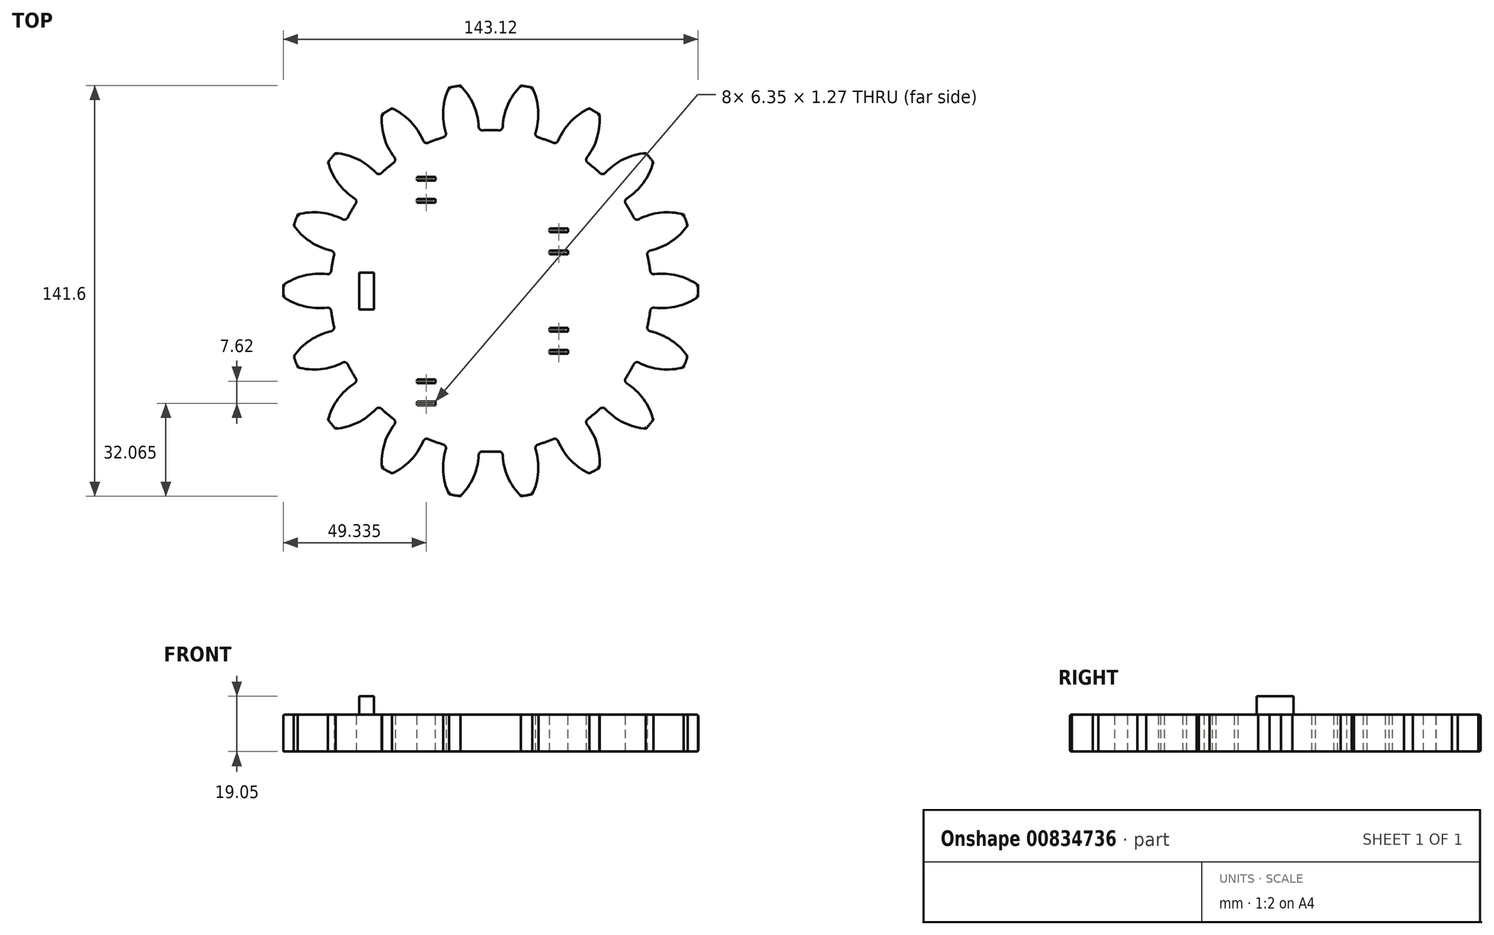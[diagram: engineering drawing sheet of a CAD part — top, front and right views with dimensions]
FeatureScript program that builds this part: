
annotation { "Feature Type Name" : "Feature", "Feature Type Description" : "" }
export const myFeature = defineFeature(function(context is Context, id is Id, definition is map)
    precondition{}
    {
        {
            var Q0;
            Q0=qCreatedBy(makeId("Top.planeOp"),FACE);
            var sketch = newSketch(context, id + "F0", { "sketchPlane" : qUnion([Q0])});
            skCircle(sketch, "E0", {"center": v(0, 0) * mm, "radius": 10.58 * mm});
            skCircle(sketch, "E1", {"center": v(0, 0) * mm, "radius": 21.17 * mm});
            skCircle(sketch, "E2", {"center": v(0, 0) * mm, "radius": 42.33 * mm});
            skArc(sketch, "E3.0", {"start": v(71.54, -1.99) * mm, "mid": v(71.56, 0) * mm, "end": v(71.54, 1.99) * mm});
            skArc(sketch, "E4.trimOffspring", {"start": v(2.79, 55.37) * mm, "mid": v(0, 55.44) * mm, "end": v(-2.79, 55.37) * mm});
            skPoint(sketch, "E5.orphan", {"position": v(0, 102.8) * mm});
            skArc(sketch, "E6.1.0", {"start": v(-16.32, 52.98) * mm, "mid": v(-18.96, 52.1) * mm, "end": v(-21.56, 51.07) * mm});
            skArc(sketch, "E6.2.0", {"start": v(-33.45, 44.2) * mm, "mid": v(-35.63, 42.47) * mm, "end": v(-37.72, 40.62) * mm});
            skArc(sketch, "E7.3.3.0", {"start": v(-46.55, 30.1) * mm, "mid": v(-48, 27.72) * mm, "end": v(-49.34, 25.27) * mm});
            skArc(sketch, "E7.3.4.0", {"start": v(-54.04, 12.36) * mm, "mid": v(-54.6, 9.63) * mm, "end": v(-55, 6.87) * mm});
            skArc(sketch, "E7.3.5.0", {"start": v(-55, -6.87) * mm, "mid": v(-54.6, -9.63) * mm, "end": v(-54.04, -12.36) * mm});
            skArc(sketch, "E7.3.6.0", {"start": v(-49.34, -25.27) * mm, "mid": v(-48, -27.72) * mm, "end": v(-46.55, -30.1) * mm});
            skArc(sketch, "E7.3.7.0", {"start": v(-37.72, -40.62) * mm, "mid": v(-35.63, -42.47) * mm, "end": v(-33.45, -44.2) * mm});
            skArc(sketch, "E7.3.8.0", {"start": v(-21.56, -51.07) * mm, "mid": v(-18.96, -52.1) * mm, "end": v(-16.32, -52.98) * mm});
            skArc(sketch, "E7.3.9.0", {"start": v(-2.79, -55.37) * mm, "mid": v(0, -55.44) * mm, "end": v(2.79, -55.37) * mm});
            skArc(sketch, "E7.3.10.0", {"start": v(16.32, -52.98) * mm, "mid": v(18.96, -52.1) * mm, "end": v(21.56, -51.07) * mm});
            skArc(sketch, "E7.3.11.0", {"start": v(33.45, -44.2) * mm, "mid": v(35.63, -42.47) * mm, "end": v(37.72, -40.62) * mm});
            skArc(sketch, "E7.3.12.0", {"start": v(46.55, -30.1) * mm, "mid": v(48, -27.72) * mm, "end": v(49.34, -25.27) * mm});
            skArc(sketch, "E7.3.13.0", {"start": v(54.04, -12.36) * mm, "mid": v(54.6, -9.63) * mm, "end": v(55, -6.87) * mm});
            skArc(sketch, "E7.3.14.0", {"start": v(55, 6.87) * mm, "mid": v(54.6, 9.63) * mm, "end": v(54.04, 12.36) * mm});
            skArc(sketch, "E7.3.15.0", {"start": v(49.34, 25.27) * mm, "mid": v(48, 27.72) * mm, "end": v(46.55, 30.1) * mm});
            skArc(sketch, "E7.3.16.0", {"start": v(37.72, 40.62) * mm, "mid": v(35.63, 42.47) * mm, "end": v(33.45, 44.2) * mm});
            skArc(sketch, "E7.3.17.0", {"start": v(21.56, 51.07) * mm, "mid": v(18.96, 52.1) * mm, "end": v(16.32, 52.98) * mm});
            skArc(sketch, "E8", {"start": v(71.54, 1.99) * mm, "mid": v(64.35, 5.3) * mm, "end": v(56.45, 5.75) * mm});
            skArc(sketch, "E9", {"start": v(56.45, -5.75) * mm, "mid": v(64.35, -5.3) * mm, "end": v(71.54, -1.99) * mm});
            skArc(sketch, "E10.1.0", {"start": v(55.02, 13.9) * mm, "mid": v(62.28, 17.03) * mm, "end": v(67.9, 22.6) * mm});
            skArc(sketch, "E10.1.1", {"start": v(67.9, 22.6) * mm, "mid": v(67.25, 24.48) * mm, "end": v(66.54, 26.34) * mm});
            skArc(sketch, "E10.1.2", {"start": v(66.54, 26.34) * mm, "mid": v(58.66, 26.99) * mm, "end": v(51.08, 24.71) * mm});
            skArc(sketch, "E10.2.0", {"start": v(46.94, 31.88) * mm, "mid": v(52.7, 37.3) * mm, "end": v(56.08, 44.46) * mm});
            skArc(sketch, "E10.2.1", {"start": v(56.08, 44.46) * mm, "mid": v(54.82, 46) * mm, "end": v(53.52, 47.5) * mm});
            skArc(sketch, "E10.2.2", {"start": v(53.52, 47.5) * mm, "mid": v(45.89, 45.42) * mm, "end": v(39.55, 40.7) * mm});
            skArc(sketch, "E10.3.0", {"start": v(33.2, 46.01) * mm, "mid": v(36.77, 53.08) * mm, "end": v(37.5, 60.96) * mm});
            skArc(sketch, "E10.3.1", {"start": v(37.5, 60.96) * mm, "mid": v(35.78, 61.98) * mm, "end": v(34.05, 62.95) * mm});
            skArc(sketch, "E10.3.2", {"start": v(34.05, 62.95) * mm, "mid": v(27.59, 58.38) * mm, "end": v(23.24, 51.77) * mm});
            skArc(sketch, "E10.4.0", {"start": v(15.47, 54.6) * mm, "mid": v(16.4, 62.45) * mm, "end": v(14.38, 70.1) * mm});
            skArc(sketch, "E10.4.1", {"start": v(14.38, 70.1) * mm, "mid": v(12.43, 70.48) * mm, "end": v(10.46, 70.8) * mm});
            skArc(sketch, "E10.4.2", {"start": v(10.46, 70.8) * mm, "mid": v(5.95, 64.3) * mm, "end": v(4.14, 56.6) * mm});
            skArc(sketch, "E10.5.0", {"start": v(-4.14, 56.6) * mm, "mid": v(-5.95, 64.3) * mm, "end": v(-10.46, 70.8) * mm});
            skArc(sketch, "E10.5.1", {"start": v(-10.46, 70.8) * mm, "mid": v(-12.43, 70.48) * mm, "end": v(-14.38, 70.1) * mm});
            skArc(sketch, "E10.5.2", {"start": v(-14.38, 70.1) * mm, "mid": v(-16.4, 62.45) * mm, "end": v(-15.47, 54.6) * mm});
            skArc(sketch, "E10.6.0", {"start": v(-23.24, 51.77) * mm, "mid": v(-27.59, 58.38) * mm, "end": v(-34.05, 62.95) * mm});
            skArc(sketch, "E10.6.1", {"start": v(-34.05, 62.95) * mm, "mid": v(-35.78, 61.98) * mm, "end": v(-37.5, 60.96) * mm});
            skArc(sketch, "E10.6.2", {"start": v(-37.5, 60.96) * mm, "mid": v(-36.77, 53.08) * mm, "end": v(-33.2, 46.01) * mm});
            skArc(sketch, "E10.7.0", {"start": v(-39.55, 40.7) * mm, "mid": v(-45.89, 45.42) * mm, "end": v(-53.52, 47.5) * mm});
            skArc(sketch, "E10.7.1", {"start": v(-53.52, 47.5) * mm, "mid": v(-54.82, 46) * mm, "end": v(-56.08, 44.46) * mm});
            skArc(sketch, "E10.7.2", {"start": v(-56.08, 44.46) * mm, "mid": v(-52.7, 37.3) * mm, "end": v(-46.94, 31.88) * mm});
            skArc(sketch, "E10.8.0", {"start": v(-51.08, 24.71) * mm, "mid": v(-58.66, 26.99) * mm, "end": v(-66.54, 26.34) * mm});
            skArc(sketch, "E10.8.1", {"start": v(-66.54, 26.34) * mm, "mid": v(-67.25, 24.48) * mm, "end": v(-67.9, 22.6) * mm});
            skArc(sketch, "E10.8.2", {"start": v(-67.9, 22.6) * mm, "mid": v(-62.28, 17.03) * mm, "end": v(-55.02, 13.9) * mm});
            skArc(sketch, "E10.9.0", {"start": v(-56.45, 5.75) * mm, "mid": v(-64.35, 5.3) * mm, "end": v(-71.54, 1.99) * mm});
            skArc(sketch, "E10.9.1", {"start": v(-71.54, 1.99) * mm, "mid": v(-71.56, 0) * mm, "end": v(-71.54, -1.99) * mm});
            skArc(sketch, "E10.9.2", {"start": v(-71.54, -1.99) * mm, "mid": v(-64.35, -5.3) * mm, "end": v(-56.45, -5.75) * mm});
            skArc(sketch, "E10.10.0", {"start": v(-55.02, -13.9) * mm, "mid": v(-62.28, -17.03) * mm, "end": v(-67.9, -22.6) * mm});
            skArc(sketch, "E10.10.1", {"start": v(-67.9, -22.6) * mm, "mid": v(-67.25, -24.48) * mm, "end": v(-66.54, -26.34) * mm});
            skArc(sketch, "E10.10.2", {"start": v(-66.54, -26.34) * mm, "mid": v(-58.66, -26.99) * mm, "end": v(-51.08, -24.71) * mm});
            skArc(sketch, "E10.11.0", {"start": v(-46.94, -31.88) * mm, "mid": v(-52.7, -37.3) * mm, "end": v(-56.08, -44.46) * mm});
            skArc(sketch, "E10.11.1", {"start": v(-56.08, -44.46) * mm, "mid": v(-54.82, -46) * mm, "end": v(-53.52, -47.5) * mm});
            skArc(sketch, "E10.11.2", {"start": v(-53.52, -47.5) * mm, "mid": v(-45.89, -45.42) * mm, "end": v(-39.55, -40.7) * mm});
            skArc(sketch, "E10.12.0", {"start": v(-33.2, -46.01) * mm, "mid": v(-36.77, -53.08) * mm, "end": v(-37.5, -60.96) * mm});
            skArc(sketch, "E10.12.1", {"start": v(-37.5, -60.96) * mm, "mid": v(-35.78, -61.98) * mm, "end": v(-34.05, -62.95) * mm});
            skArc(sketch, "E10.12.2", {"start": v(-34.05, -62.95) * mm, "mid": v(-27.59, -58.38) * mm, "end": v(-23.24, -51.77) * mm});
            skArc(sketch, "E10.13.0", {"start": v(-15.47, -54.6) * mm, "mid": v(-16.4, -62.45) * mm, "end": v(-14.38, -70.1) * mm});
            skArc(sketch, "E10.13.1", {"start": v(-14.38, -70.1) * mm, "mid": v(-12.43, -70.48) * mm, "end": v(-10.46, -70.8) * mm});
            skArc(sketch, "E10.13.2", {"start": v(-10.46, -70.8) * mm, "mid": v(-5.95, -64.3) * mm, "end": v(-4.14, -56.6) * mm});
            skArc(sketch, "E10.14.0", {"start": v(4.14, -56.6) * mm, "mid": v(5.95, -64.3) * mm, "end": v(10.46, -70.8) * mm});
            skArc(sketch, "E10.14.1", {"start": v(10.46, -70.8) * mm, "mid": v(12.43, -70.48) * mm, "end": v(14.38, -70.1) * mm});
            skArc(sketch, "E10.14.2", {"start": v(14.38, -70.1) * mm, "mid": v(16.4, -62.45) * mm, "end": v(15.47, -54.6) * mm});
            skArc(sketch, "E10.15.0", {"start": v(23.24, -51.77) * mm, "mid": v(27.59, -58.38) * mm, "end": v(34.05, -62.95) * mm});
            skArc(sketch, "E10.15.1", {"start": v(34.05, -62.95) * mm, "mid": v(35.78, -61.98) * mm, "end": v(37.5, -60.96) * mm});
            skArc(sketch, "E10.15.2", {"start": v(37.5, -60.96) * mm, "mid": v(36.77, -53.08) * mm, "end": v(33.2, -46.01) * mm});
            skArc(sketch, "E10.16.0", {"start": v(39.55, -40.7) * mm, "mid": v(45.89, -45.42) * mm, "end": v(53.52, -47.5) * mm});
            skArc(sketch, "E10.16.1", {"start": v(53.52, -47.5) * mm, "mid": v(54.82, -46) * mm, "end": v(56.08, -44.46) * mm});
            skArc(sketch, "E10.16.2", {"start": v(56.08, -44.46) * mm, "mid": v(52.7, -37.3) * mm, "end": v(46.94, -31.88) * mm});
            skArc(sketch, "E10.17.0", {"start": v(51.08, -24.71) * mm, "mid": v(58.66, -26.99) * mm, "end": v(66.54, -26.34) * mm});
            skArc(sketch, "E10.17.1", {"start": v(66.54, -26.34) * mm, "mid": v(67.25, -24.48) * mm, "end": v(67.9, -22.6) * mm});
            skArc(sketch, "E10.17.2", {"start": v(67.9, -22.6) * mm, "mid": v(62.28, -17.03) * mm, "end": v(55.02, -13.9) * mm});
            skPoint(sketch, "E11.newPointA", {"position": v(15.04, 53.36) * mm});
            skPoint(sketch, "E11.newPointB", {"position": v(14.64, 53.47) * mm});
            skArc(sketch, "E11.filletArc", {"start": v(15.47, 54.6) * mm, "mid": v(15.56, 53.61) * mm, "end": v(16.32, 52.98) * mm});
            skPoint(sketch, "E12.newPointA", {"position": v(22.78, 50.54) * mm});
            skPoint(sketch, "E12.newPointB", {"position": v(23.15, 50.37) * mm});
            skArc(sketch, "E12.filletArc", {"start": v(21.56, 51.07) * mm, "mid": v(22.54, 51.07) * mm, "end": v(23.24, 51.77) * mm});
            skPoint(sketch, "E13.newPointA", {"position": v(32.38, 45) * mm});
            skPoint(sketch, "E13.newPointB", {"position": v(32.04, 45.24) * mm});
            skArc(sketch, "E13.filletArc", {"start": v(33.2, 46.01) * mm, "mid": v(32.95, 45.06) * mm, "end": v(33.45, 44.2) * mm});
            skPoint(sketch, "E14.newPointA", {"position": v(38.7, 39.7) * mm});
            skPoint(sketch, "E14.newPointB", {"position": v(38.98, 39.41) * mm});
            skArc(sketch, "E14.filletArc", {"start": v(37.72, 40.62) * mm, "mid": v(38.65, 40.28) * mm, "end": v(39.55, 40.7) * mm});
            skPoint(sketch, "E15.newPointA", {"position": v(45.82, 31.2) * mm});
            skPoint(sketch, "E15.newPointB", {"position": v(45.58, 31.55) * mm});
            skArc(sketch, "E15.filletArc", {"start": v(46.94, 31.88) * mm, "mid": v(46.38, 31.07) * mm, "end": v(46.55, 30.1) * mm});
            skPoint(sketch, "E16.newPointA", {"position": v(50.11, 23.7) * mm});
            skPoint(sketch, "E16.newPointB", {"position": v(49.94, 24.07) * mm});
            skArc(sketch, "E16.filletArc", {"start": v(49.34, 25.27) * mm, "mid": v(50.1, 24.63) * mm, "end": v(51.08, 24.71) * mm});
            skPoint(sketch, "E17.newPointA", {"position": v(53.73, 13.66) * mm});
            skPoint(sketch, "E17.newPointB", {"position": v(53.62, 14.05) * mm});
            skArc(sketch, "E17.filletArc", {"start": v(55.02, 13.9) * mm, "mid": v(54.2, 13.33) * mm, "end": v(54.04, 12.36) * mm});
            skPoint(sketch, "E18.newPointA", {"position": v(55.16, 5.54) * mm});
            skPoint(sketch, "E18.newPointB", {"position": v(55.2, 5.13) * mm});
            skArc(sketch, "E18.filletArc", {"start": v(55, 6.87) * mm, "mid": v(55.5, 6.01) * mm, "end": v(56.45, 5.75) * mm});
            skPoint(sketch, "E19.newPointA", {"position": v(55.16, -5.54) * mm});
            skPoint(sketch, "E19.newPointB", {"position": v(55.2, -5.13) * mm});
            skArc(sketch, "E19.filletArc", {"start": v(56.45, -5.75) * mm, "mid": v(55.5, -6.01) * mm, "end": v(55, -6.87) * mm});
            skPoint(sketch, "E20.newPointA", {"position": v(53.73, -13.66) * mm});
            skPoint(sketch, "E20.newPointB", {"position": v(53.62, -14.05) * mm});
            skArc(sketch, "E20.filletArc", {"start": v(54.04, -12.36) * mm, "mid": v(54.2, -13.33) * mm, "end": v(55.02, -13.9) * mm});
            skPoint(sketch, "E21.newPointA", {"position": v(49.94, -24.07) * mm});
            skPoint(sketch, "E21.newPointB", {"position": v(50.11, -23.7) * mm});
            skArc(sketch, "E21.filletArc", {"start": v(51.08, -24.71) * mm, "mid": v(50.1, -24.63) * mm, "end": v(49.34, -25.27) * mm});
            skPoint(sketch, "E22.newPointA", {"position": v(45.82, -31.2) * mm});
            skPoint(sketch, "E22.newPointB", {"position": v(45.58, -31.55) * mm});
            skArc(sketch, "E22.filletArc", {"start": v(46.55, -30.1) * mm, "mid": v(46.38, -31.07) * mm, "end": v(46.94, -31.88) * mm});
            skPoint(sketch, "E23.newPointA", {"position": v(38.7, -39.7) * mm});
            skPoint(sketch, "E23.newPointB", {"position": v(38.98, -39.41) * mm});
            skArc(sketch, "E23.filletArc", {"start": v(39.55, -40.7) * mm, "mid": v(38.65, -40.28) * mm, "end": v(37.72, -40.62) * mm});
            skPoint(sketch, "E24.newPointA", {"position": v(32.38, -45) * mm});
            skPoint(sketch, "E24.newPointB", {"position": v(32.04, -45.24) * mm});
            skArc(sketch, "E24.filletArc", {"start": v(33.45, -44.2) * mm, "mid": v(32.95, -45.06) * mm, "end": v(33.2, -46.01) * mm});
            skPoint(sketch, "E25.newPointA", {"position": v(22.78, -50.54) * mm});
            skPoint(sketch, "E25.newPointB", {"position": v(23.15, -50.37) * mm});
            skArc(sketch, "E25.filletArc", {"start": v(23.24, -51.77) * mm, "mid": v(22.54, -51.07) * mm, "end": v(21.56, -51.07) * mm});
            skPoint(sketch, "E26.newPointA", {"position": v(15.04, -53.36) * mm});
            skPoint(sketch, "E26.newPointB", {"position": v(14.64, -53.47) * mm});
            skArc(sketch, "E26.filletArc", {"start": v(16.32, -52.98) * mm, "mid": v(15.56, -53.61) * mm, "end": v(15.47, -54.6) * mm});
            skPoint(sketch, "E27.newPointA", {"position": v(4.12, -55.28) * mm});
            skPoint(sketch, "E27.newPointB", {"position": v(4.53, -55.25) * mm});
            skArc(sketch, "E27.filletArc", {"start": v(4.14, -56.6) * mm, "mid": v(3.72, -55.7) * mm, "end": v(2.79, -55.37) * mm});
            skPoint(sketch, "E28.newPointA", {"position": v(-4.12, -55.28) * mm});
            skPoint(sketch, "E28.newPointB", {"position": v(-4.53, -55.25) * mm});
            skArc(sketch, "E28.filletArc", {"start": v(-2.79, -55.37) * mm, "mid": v(-3.72, -55.7) * mm, "end": v(-4.14, -56.6) * mm});
            skPoint(sketch, "E29.newPointA", {"position": v(-15.04, -53.36) * mm});
            skPoint(sketch, "E29.newPointB", {"position": v(-14.64, -53.47) * mm});
            skArc(sketch, "E29.filletArc", {"start": v(-15.47, -54.6) * mm, "mid": v(-15.56, -53.61) * mm, "end": v(-16.32, -52.98) * mm});
            skPoint(sketch, "E30.newPointA", {"position": v(-22.78, -50.54) * mm});
            skPoint(sketch, "E30.newPointB", {"position": v(-23.15, -50.37) * mm});
            skArc(sketch, "E30.filletArc", {"start": v(-21.56, -51.07) * mm, "mid": v(-22.54, -51.07) * mm, "end": v(-23.24, -51.77) * mm});
            skPoint(sketch, "E31.newPointA", {"position": v(-32.38, -45) * mm});
            skPoint(sketch, "E31.newPointB", {"position": v(-32.04, -45.24) * mm});
            skArc(sketch, "E31.filletArc", {"start": v(-33.2, -46.01) * mm, "mid": v(-32.95, -45.06) * mm, "end": v(-33.45, -44.2) * mm});
            skPoint(sketch, "E32.newPointA", {"position": v(-38.98, -39.41) * mm});
            skPoint(sketch, "E32.newPointB", {"position": v(-38.7, -39.7) * mm});
            skArc(sketch, "E32.filletArc", {"start": v(-37.72, -40.62) * mm, "mid": v(-38.65, -40.28) * mm, "end": v(-39.55, -40.7) * mm});
            skPoint(sketch, "E33.newPointA", {"position": v(-45.82, -31.2) * mm});
            skPoint(sketch, "E33.newPointB", {"position": v(-45.58, -31.55) * mm});
            skArc(sketch, "E33.filletArc", {"start": v(-46.94, -31.88) * mm, "mid": v(-46.38, -31.07) * mm, "end": v(-46.55, -30.1) * mm});
            skPoint(sketch, "E34.newPointA", {"position": v(-49.94, -24.07) * mm});
            skPoint(sketch, "E34.newPointB", {"position": v(-50.11, -23.7) * mm});
            skArc(sketch, "E34.filletArc", {"start": v(-49.34, -25.27) * mm, "mid": v(-50.1, -24.63) * mm, "end": v(-51.08, -24.71) * mm});
            skPoint(sketch, "E35.newPointA", {"position": v(-53.73, -13.66) * mm});
            skPoint(sketch, "E35.newPointB", {"position": v(-53.62, -14.05) * mm});
            skArc(sketch, "E35.filletArc", {"start": v(-55.02, -13.9) * mm, "mid": v(-54.2, -13.33) * mm, "end": v(-54.04, -12.36) * mm});
            skPoint(sketch, "E36.newPointA", {"position": v(-55.2, -5.13) * mm});
            skPoint(sketch, "E36.newPointB", {"position": v(-55.16, -5.54) * mm});
            skArc(sketch, "E36.filletArc", {"start": v(-55, -6.87) * mm, "mid": v(-55.5, -6.01) * mm, "end": v(-56.45, -5.75) * mm});
            skPoint(sketch, "E37.newPointA", {"position": v(-55.16, 5.54) * mm});
            skPoint(sketch, "E37.newPointB", {"position": v(-55.2, 5.13) * mm});
            skArc(sketch, "E37.filletArc", {"start": v(-56.45, 5.75) * mm, "mid": v(-55.5, 6.01) * mm, "end": v(-55, 6.87) * mm});
            skPoint(sketch, "E38.newPointA", {"position": v(-53.73, 13.66) * mm});
            skPoint(sketch, "E38.newPointB", {"position": v(-53.62, 14.05) * mm});
            skArc(sketch, "E38.filletArc", {"start": v(-54.04, 12.36) * mm, "mid": v(-54.2, 13.33) * mm, "end": v(-55.02, 13.9) * mm});
            skPoint(sketch, "E39.newPointA", {"position": v(-49.94, 24.07) * mm});
            skPoint(sketch, "E39.newPointB", {"position": v(-50.11, 23.7) * mm});
            skArc(sketch, "E39.filletArc", {"start": v(-51.08, 24.71) * mm, "mid": v(-50.1, 24.63) * mm, "end": v(-49.34, 25.27) * mm});
            skPoint(sketch, "E40.newPointA", {"position": v(-45.82, 31.2) * mm});
            skPoint(sketch, "E40.newPointB", {"position": v(-45.58, 31.55) * mm});
            skArc(sketch, "E40.filletArc", {"start": v(-46.55, 30.1) * mm, "mid": v(-46.38, 31.07) * mm, "end": v(-46.94, 31.88) * mm});
            skPoint(sketch, "E41.newPointA", {"position": v(-38.7, 39.7) * mm});
            skPoint(sketch, "E41.newPointB", {"position": v(-38.98, 39.41) * mm});
            skArc(sketch, "E41.filletArc", {"start": v(-39.55, 40.7) * mm, "mid": v(-38.65, 40.28) * mm, "end": v(-37.72, 40.62) * mm});
            skPoint(sketch, "E42.newPointA", {"position": v(-32.38, 45) * mm});
            skPoint(sketch, "E42.newPointB", {"position": v(-32.04, 45.24) * mm});
            skArc(sketch, "E42.filletArc", {"start": v(-33.45, 44.2) * mm, "mid": v(-32.95, 45.06) * mm, "end": v(-33.2, 46.01) * mm});
            skPoint(sketch, "E43.newPointA", {"position": v(-22.78, 50.54) * mm});
            skPoint(sketch, "E43.newPointB", {"position": v(-23.15, 50.37) * mm});
            skArc(sketch, "E43.filletArc", {"start": v(-23.24, 51.77) * mm, "mid": v(-22.54, 51.07) * mm, "end": v(-21.56, 51.07) * mm});
            skPoint(sketch, "E44.newPointA", {"position": v(-15.04, 53.36) * mm});
            skPoint(sketch, "E44.newPointB", {"position": v(-14.64, 53.47) * mm});
            skArc(sketch, "E44.filletArc", {"start": v(-16.32, 52.98) * mm, "mid": v(-15.56, 53.61) * mm, "end": v(-15.47, 54.6) * mm});
            skPoint(sketch, "E45.newPointA", {"position": v(-4.12, 55.28) * mm});
            skPoint(sketch, "E45.newPointB", {"position": v(-4.53, 55.25) * mm});
            skArc(sketch, "E45.filletArc", {"start": v(-4.14, 56.6) * mm, "mid": v(-3.72, 55.7) * mm, "end": v(-2.79, 55.37) * mm});
            skPoint(sketch, "E46.newPointA", {"position": v(4.12, 55.28) * mm});
            skPoint(sketch, "E46.newPointB", {"position": v(4.53, 55.25) * mm});
            skArc(sketch, "E46.filletArc", {"start": v(2.79, 55.37) * mm, "mid": v(3.72, 55.7) * mm, "end": v(4.14, 56.6) * mm});
            skSolve(sketch);
        }
        {
            var Q0;
            Q0=makeQuery(id+"F0.imprint","IMPRINT",FACE,{"disambiguationData":[TD([[makeQuery(id+"F0.imprint","IMPRINT",EDGE,{"derivedFrom":sQuery(id+"F0.wireOp",EDGE,"E2")}),-1.0]])]});
            extrude(context, id + "F1", {"entities" : qUnion([Q0]), "depth" : 12.7 * mm, "offsetDistance" : 25.4 * mm});
        }
        {
            var Q0;
            Q0=qCreatedBy(makeId("Top.planeOp"),FACE);
            var sketch = newSketch(context, id + "F2", { "sketchPlane" : qUnion([Q0])});
            skCircle(sketch, "E47", {"center": v(0, 0) * mm, "radius": 42.33 * mm});
            skSolve(sketch);
        }
        {
            var Q0;
            Q0=makeQuery(id+"F2.imprint","IMPRINT",FACE,{"disambiguationData":[TD([[makeQuery(id+"F2.imprint","IMPRINT",EDGE,{"derivedFrom":sQuery(id+"F2.wireOp",EDGE,"E47")}),1.0]])]});
            extrude(context, id + "F3", {"entities" : qUnion([Q0]), "operationType" : NewBodyOperationType.ADD, "depth" : 12.7 * mm, "offsetDistance" : 25.4 * mm});
        }
        {
            var Q0;
            Q0=makeQuery(id+"F1.opExtrude","CAP_FACE",FACE,{"disambiguationData":[OSD([sQuery(id+"F0.wireOp",EDGE,"E2"),sQuery(id+"F0.wireOp",EDGE,"E3.0"),sQuery(id+"F0.wireOp",EDGE,"E4.trimOffspring"),sQuery(id+"F0.wireOp",EDGE,"E6.1.0"),sQuery(id+"F0.wireOp",EDGE,"E6.2.0"),sQuery(id+"F0.wireOp",EDGE,"E7.3.3.0"),sQuery(id+"F0.wireOp",EDGE,"E7.3.4.0"),sQuery(id+"F0.wireOp",EDGE,"E7.3.5.0"),sQuery(id+"F0.wireOp",EDGE,"E7.3.6.0"),sQuery(id+"F0.wireOp",EDGE,"E7.3.7.0"),sQuery(id+"F0.wireOp",EDGE,"E7.3.8.0"),sQuery(id+"F0.wireOp",EDGE,"E7.3.9.0"),sQuery(id+"F0.wireOp",EDGE,"E7.3.10.0"),sQuery(id+"F0.wireOp",EDGE,"E7.3.11.0"),sQuery(id+"F0.wireOp",EDGE,"E7.3.12.0"),sQuery(id+"F0.wireOp",EDGE,"E7.3.13.0"),sQuery(id+"F0.wireOp",EDGE,"E7.3.14.0"),sQuery(id+"F0.wireOp",EDGE,"E7.3.15.0"),sQuery(id+"F0.wireOp",EDGE,"E7.3.16.0"),sQuery(id+"F0.wireOp",EDGE,"E7.3.17.0"),sQuery(id+"F0.wireOp",EDGE,"E8"),sQuery(id+"F0.wireOp",EDGE,"E9"),sQuery(id+"F0.wireOp",EDGE,"E10.1.0"),sQuery(id+"F0.wireOp",EDGE,"E10.1.1"),sQuery(id+"F0.wireOp",EDGE,"E10.1.2"),sQuery(id+"F0.wireOp",EDGE,"E10.2.0"),sQuery(id+"F0.wireOp",EDGE,"E10.2.1"),sQuery(id+"F0.wireOp",EDGE,"E10.2.2"),sQuery(id+"F0.wireOp",EDGE,"E10.3.0"),sQuery(id+"F0.wireOp",EDGE,"E10.3.1"),sQuery(id+"F0.wireOp",EDGE,"E10.3.2"),sQuery(id+"F0.wireOp",EDGE,"E10.4.0"),sQuery(id+"F0.wireOp",EDGE,"E10.4.1"),sQuery(id+"F0.wireOp",EDGE,"E10.4.2"),sQuery(id+"F0.wireOp",EDGE,"E10.5.0"),sQuery(id+"F0.wireOp",EDGE,"E10.5.1"),sQuery(id+"F0.wireOp",EDGE,"E10.5.2"),sQuery(id+"F0.wireOp",EDGE,"E10.6.0"),sQuery(id+"F0.wireOp",EDGE,"E10.6.1"),sQuery(id+"F0.wireOp",EDGE,"E10.6.2"),sQuery(id+"F0.wireOp",EDGE,"E10.7.0"),sQuery(id+"F0.wireOp",EDGE,"E10.7.1"),sQuery(id+"F0.wireOp",EDGE,"E10.7.2"),sQuery(id+"F0.wireOp",EDGE,"E10.8.0"),sQuery(id+"F0.wireOp",EDGE,"E10.8.1"),sQuery(id+"F0.wireOp",EDGE,"E10.8.2"),sQuery(id+"F0.wireOp",EDGE,"E10.9.0"),sQuery(id+"F0.wireOp",EDGE,"E10.9.1"),sQuery(id+"F0.wireOp",EDGE,"E10.9.2"),sQuery(id+"F0.wireOp",EDGE,"E10.10.0"),sQuery(id+"F0.wireOp",EDGE,"E10.10.1"),sQuery(id+"F0.wireOp",EDGE,"E10.10.2"),sQuery(id+"F0.wireOp",EDGE,"E10.11.0"),sQuery(id+"F0.wireOp",EDGE,"E10.11.1"),sQuery(id+"F0.wireOp",EDGE,"E10.11.2"),sQuery(id+"F0.wireOp",EDGE,"E10.12.0"),sQuery(id+"F0.wireOp",EDGE,"E10.12.1"),sQuery(id+"F0.wireOp",EDGE,"E10.12.2"),sQuery(id+"F0.wireOp",EDGE,"E10.13.0"),sQuery(id+"F0.wireOp",EDGE,"E10.13.1"),sQuery(id+"F0.wireOp",EDGE,"E10.13.2"),sQuery(id+"F0.wireOp",EDGE,"E10.14.0"),sQuery(id+"F0.wireOp",EDGE,"E10.14.1"),sQuery(id+"F0.wireOp",EDGE,"E10.14.2"),sQuery(id+"F0.wireOp",EDGE,"E10.15.0"),sQuery(id+"F0.wireOp",EDGE,"E10.15.1"),sQuery(id+"F0.wireOp",EDGE,"E10.15.2"),sQuery(id+"F0.wireOp",EDGE,"E10.16.0"),sQuery(id+"F0.wireOp",EDGE,"E10.16.1"),sQuery(id+"F0.wireOp",EDGE,"E10.16.2"),sQuery(id+"F0.wireOp",EDGE,"E10.17.0"),sQuery(id+"F0.wireOp",EDGE,"E10.17.1"),sQuery(id+"F0.wireOp",EDGE,"E10.17.2"),sQuery(id+"F0.wireOp",EDGE,"E11.filletArc"),sQuery(id+"F0.wireOp",EDGE,"E12.filletArc"),sQuery(id+"F0.wireOp",EDGE,"E13.filletArc"),sQuery(id+"F0.wireOp",EDGE,"E14.filletArc"),sQuery(id+"F0.wireOp",EDGE,"E15.filletArc"),sQuery(id+"F0.wireOp",EDGE,"E16.filletArc"),sQuery(id+"F0.wireOp",EDGE,"E17.filletArc"),sQuery(id+"F0.wireOp",EDGE,"E18.filletArc"),sQuery(id+"F0.wireOp",EDGE,"E19.filletArc"),sQuery(id+"F0.wireOp",EDGE,"E20.filletArc"),sQuery(id+"F0.wireOp",EDGE,"E21.filletArc"),sQuery(id+"F0.wireOp",EDGE,"E22.filletArc"),sQuery(id+"F0.wireOp",EDGE,"E23.filletArc"),sQuery(id+"F0.wireOp",EDGE,"E24.filletArc"),sQuery(id+"F0.wireOp",EDGE,"E25.filletArc"),sQuery(id+"F0.wireOp",EDGE,"E26.filletArc"),sQuery(id+"F0.wireOp",EDGE,"E27.filletArc"),sQuery(id+"F0.wireOp",EDGE,"E28.filletArc"),sQuery(id+"F0.wireOp",EDGE,"E29.filletArc"),sQuery(id+"F0.wireOp",EDGE,"E30.filletArc"),sQuery(id+"F0.wireOp",EDGE,"E31.filletArc"),sQuery(id+"F0.wireOp",EDGE,"E32.filletArc"),sQuery(id+"F0.wireOp",EDGE,"E33.filletArc"),sQuery(id+"F0.wireOp",EDGE,"E34.filletArc"),sQuery(id+"F0.wireOp",EDGE,"E35.filletArc"),sQuery(id+"F0.wireOp",EDGE,"E36.filletArc"),sQuery(id+"F0.wireOp",EDGE,"E37.filletArc"),sQuery(id+"F0.wireOp",EDGE,"E38.filletArc"),sQuery(id+"F0.wireOp",EDGE,"E39.filletArc"),sQuery(id+"F0.wireOp",EDGE,"E40.filletArc"),sQuery(id+"F0.wireOp",EDGE,"E41.filletArc"),sQuery(id+"F0.wireOp",EDGE,"E42.filletArc"),sQuery(id+"F0.wireOp",EDGE,"E43.filletArc"),sQuery(id+"F0.wireOp",EDGE,"E44.filletArc"),sQuery(id+"F0.wireOp",EDGE,"E45.filletArc"),sQuery(id+"F0.wireOp",EDGE,"E46.filletArc")])],"isStart":false});
            var Q1;
            Q1=makeQuery(id+"F1.opExtrude","CAP_FACE",FACE,{"disambiguationData":[OSD([sQuery(id+"F0.wireOp",EDGE,"E2"),sQuery(id+"F0.wireOp",EDGE,"E3.0"),sQuery(id+"F0.wireOp",EDGE,"E4.trimOffspring"),sQuery(id+"F0.wireOp",EDGE,"E6.1.0"),sQuery(id+"F0.wireOp",EDGE,"E6.2.0"),sQuery(id+"F0.wireOp",EDGE,"E7.3.3.0"),sQuery(id+"F0.wireOp",EDGE,"E7.3.4.0"),sQuery(id+"F0.wireOp",EDGE,"E7.3.5.0"),sQuery(id+"F0.wireOp",EDGE,"E7.3.6.0"),sQuery(id+"F0.wireOp",EDGE,"E7.3.7.0"),sQuery(id+"F0.wireOp",EDGE,"E7.3.8.0"),sQuery(id+"F0.wireOp",EDGE,"E7.3.9.0"),sQuery(id+"F0.wireOp",EDGE,"E7.3.10.0"),sQuery(id+"F0.wireOp",EDGE,"E7.3.11.0"),sQuery(id+"F0.wireOp",EDGE,"E7.3.12.0"),sQuery(id+"F0.wireOp",EDGE,"E7.3.13.0"),sQuery(id+"F0.wireOp",EDGE,"E7.3.14.0"),sQuery(id+"F0.wireOp",EDGE,"E7.3.15.0"),sQuery(id+"F0.wireOp",EDGE,"E7.3.16.0"),sQuery(id+"F0.wireOp",EDGE,"E7.3.17.0"),sQuery(id+"F0.wireOp",EDGE,"E8"),sQuery(id+"F0.wireOp",EDGE,"E9"),sQuery(id+"F0.wireOp",EDGE,"E10.1.0"),sQuery(id+"F0.wireOp",EDGE,"E10.1.1"),sQuery(id+"F0.wireOp",EDGE,"E10.1.2"),sQuery(id+"F0.wireOp",EDGE,"E10.2.0"),sQuery(id+"F0.wireOp",EDGE,"E10.2.1"),sQuery(id+"F0.wireOp",EDGE,"E10.2.2"),sQuery(id+"F0.wireOp",EDGE,"E10.3.0"),sQuery(id+"F0.wireOp",EDGE,"E10.3.1"),sQuery(id+"F0.wireOp",EDGE,"E10.3.2"),sQuery(id+"F0.wireOp",EDGE,"E10.4.0"),sQuery(id+"F0.wireOp",EDGE,"E10.4.1"),sQuery(id+"F0.wireOp",EDGE,"E10.4.2"),sQuery(id+"F0.wireOp",EDGE,"E10.5.0"),sQuery(id+"F0.wireOp",EDGE,"E10.5.1"),sQuery(id+"F0.wireOp",EDGE,"E10.5.2"),sQuery(id+"F0.wireOp",EDGE,"E10.6.0"),sQuery(id+"F0.wireOp",EDGE,"E10.6.1"),sQuery(id+"F0.wireOp",EDGE,"E10.6.2"),sQuery(id+"F0.wireOp",EDGE,"E10.7.0"),sQuery(id+"F0.wireOp",EDGE,"E10.7.1"),sQuery(id+"F0.wireOp",EDGE,"E10.7.2"),sQuery(id+"F0.wireOp",EDGE,"E10.8.0"),sQuery(id+"F0.wireOp",EDGE,"E10.8.1"),sQuery(id+"F0.wireOp",EDGE,"E10.8.2"),sQuery(id+"F0.wireOp",EDGE,"E10.9.0"),sQuery(id+"F0.wireOp",EDGE,"E10.9.1"),sQuery(id+"F0.wireOp",EDGE,"E10.9.2"),sQuery(id+"F0.wireOp",EDGE,"E10.10.0"),sQuery(id+"F0.wireOp",EDGE,"E10.10.1"),sQuery(id+"F0.wireOp",EDGE,"E10.10.2"),sQuery(id+"F0.wireOp",EDGE,"E10.11.0"),sQuery(id+"F0.wireOp",EDGE,"E10.11.1"),sQuery(id+"F0.wireOp",EDGE,"E10.11.2"),sQuery(id+"F0.wireOp",EDGE,"E10.12.0"),sQuery(id+"F0.wireOp",EDGE,"E10.12.1"),sQuery(id+"F0.wireOp",EDGE,"E10.12.2"),sQuery(id+"F0.wireOp",EDGE,"E10.13.0"),sQuery(id+"F0.wireOp",EDGE,"E10.13.1"),sQuery(id+"F0.wireOp",EDGE,"E10.13.2"),sQuery(id+"F0.wireOp",EDGE,"E10.14.0"),sQuery(id+"F0.wireOp",EDGE,"E10.14.1"),sQuery(id+"F0.wireOp",EDGE,"E10.14.2"),sQuery(id+"F0.wireOp",EDGE,"E10.15.0"),sQuery(id+"F0.wireOp",EDGE,"E10.15.1"),sQuery(id+"F0.wireOp",EDGE,"E10.15.2"),sQuery(id+"F0.wireOp",EDGE,"E10.16.0"),sQuery(id+"F0.wireOp",EDGE,"E10.16.1"),sQuery(id+"F0.wireOp",EDGE,"E10.16.2"),sQuery(id+"F0.wireOp",EDGE,"E10.17.0"),sQuery(id+"F0.wireOp",EDGE,"E10.17.1"),sQuery(id+"F0.wireOp",EDGE,"E10.17.2"),sQuery(id+"F0.wireOp",EDGE,"E11.filletArc"),sQuery(id+"F0.wireOp",EDGE,"E12.filletArc"),sQuery(id+"F0.wireOp",EDGE,"E13.filletArc"),sQuery(id+"F0.wireOp",EDGE,"E14.filletArc"),sQuery(id+"F0.wireOp",EDGE,"E15.filletArc"),sQuery(id+"F0.wireOp",EDGE,"E16.filletArc"),sQuery(id+"F0.wireOp",EDGE,"E17.filletArc"),sQuery(id+"F0.wireOp",EDGE,"E18.filletArc"),sQuery(id+"F0.wireOp",EDGE,"E19.filletArc"),sQuery(id+"F0.wireOp",EDGE,"E20.filletArc"),sQuery(id+"F0.wireOp",EDGE,"E21.filletArc"),sQuery(id+"F0.wireOp",EDGE,"E22.filletArc"),sQuery(id+"F0.wireOp",EDGE,"E23.filletArc"),sQuery(id+"F0.wireOp",EDGE,"E24.filletArc"),sQuery(id+"F0.wireOp",EDGE,"E25.filletArc"),sQuery(id+"F0.wireOp",EDGE,"E26.filletArc"),sQuery(id+"F0.wireOp",EDGE,"E27.filletArc"),sQuery(id+"F0.wireOp",EDGE,"E28.filletArc"),sQuery(id+"F0.wireOp",EDGE,"E29.filletArc"),sQuery(id+"F0.wireOp",EDGE,"E30.filletArc"),sQuery(id+"F0.wireOp",EDGE,"E31.filletArc"),sQuery(id+"F0.wireOp",EDGE,"E32.filletArc"),sQuery(id+"F0.wireOp",EDGE,"E33.filletArc"),sQuery(id+"F0.wireOp",EDGE,"E34.filletArc"),sQuery(id+"F0.wireOp",EDGE,"E35.filletArc"),sQuery(id+"F0.wireOp",EDGE,"E36.filletArc"),sQuery(id+"F0.wireOp",EDGE,"E37.filletArc"),sQuery(id+"F0.wireOp",EDGE,"E38.filletArc"),sQuery(id+"F0.wireOp",EDGE,"E39.filletArc"),sQuery(id+"F0.wireOp",EDGE,"E40.filletArc"),sQuery(id+"F0.wireOp",EDGE,"E41.filletArc"),sQuery(id+"F0.wireOp",EDGE,"E42.filletArc"),sQuery(id+"F0.wireOp",EDGE,"E43.filletArc"),sQuery(id+"F0.wireOp",EDGE,"E44.filletArc"),sQuery(id+"F0.wireOp",EDGE,"E45.filletArc"),sQuery(id+"F0.wireOp",EDGE,"E46.filletArc")])],"isStart":true});
            fillet(context, id + "F4", {"entities" : qUnion([Q0, Q1]), "radius" : 0.5 * mm, "tangentPropagation" : true, "allowEdgeOverflow" : false});
        }
        {
            var Q0;
            Q0=makeQuery(id+"F3.boolean.opBoolean","MERGE",FACE,{"derivedFrom":[makeQuery(id+"F1.opExtrude","CAP_FACE",FACE,{"disambiguationData":[OSD([sQuery(id+"F0.wireOp",EDGE,"E2"),sQuery(id+"F0.wireOp",EDGE,"E3.0"),sQuery(id+"F0.wireOp",EDGE,"E4.trimOffspring"),sQuery(id+"F0.wireOp",EDGE,"E6.1.0"),sQuery(id+"F0.wireOp",EDGE,"E6.2.0"),sQuery(id+"F0.wireOp",EDGE,"E7.3.3.0"),sQuery(id+"F0.wireOp",EDGE,"E7.3.4.0"),sQuery(id+"F0.wireOp",EDGE,"E7.3.5.0"),sQuery(id+"F0.wireOp",EDGE,"E7.3.6.0"),sQuery(id+"F0.wireOp",EDGE,"E7.3.7.0"),sQuery(id+"F0.wireOp",EDGE,"E7.3.8.0"),sQuery(id+"F0.wireOp",EDGE,"E7.3.9.0"),sQuery(id+"F0.wireOp",EDGE,"E7.3.10.0"),sQuery(id+"F0.wireOp",EDGE,"E7.3.11.0"),sQuery(id+"F0.wireOp",EDGE,"E7.3.12.0"),sQuery(id+"F0.wireOp",EDGE,"E7.3.13.0"),sQuery(id+"F0.wireOp",EDGE,"E7.3.14.0"),sQuery(id+"F0.wireOp",EDGE,"E7.3.15.0"),sQuery(id+"F0.wireOp",EDGE,"E7.3.16.0"),sQuery(id+"F0.wireOp",EDGE,"E7.3.17.0"),sQuery(id+"F0.wireOp",EDGE,"E8"),sQuery(id+"F0.wireOp",EDGE,"E9"),sQuery(id+"F0.wireOp",EDGE,"E10.1.0"),sQuery(id+"F0.wireOp",EDGE,"E10.1.1"),sQuery(id+"F0.wireOp",EDGE,"E10.1.2"),sQuery(id+"F0.wireOp",EDGE,"E10.2.0"),sQuery(id+"F0.wireOp",EDGE,"E10.2.1"),sQuery(id+"F0.wireOp",EDGE,"E10.2.2"),sQuery(id+"F0.wireOp",EDGE,"E10.3.0"),sQuery(id+"F0.wireOp",EDGE,"E10.3.1"),sQuery(id+"F0.wireOp",EDGE,"E10.3.2"),sQuery(id+"F0.wireOp",EDGE,"E10.4.0"),sQuery(id+"F0.wireOp",EDGE,"E10.4.1"),sQuery(id+"F0.wireOp",EDGE,"E10.4.2"),sQuery(id+"F0.wireOp",EDGE,"E10.5.0"),sQuery(id+"F0.wireOp",EDGE,"E10.5.1"),sQuery(id+"F0.wireOp",EDGE,"E10.5.2"),sQuery(id+"F0.wireOp",EDGE,"E10.6.0"),sQuery(id+"F0.wireOp",EDGE,"E10.6.1"),sQuery(id+"F0.wireOp",EDGE,"E10.6.2"),sQuery(id+"F0.wireOp",EDGE,"E10.7.0"),sQuery(id+"F0.wireOp",EDGE,"E10.7.1"),sQuery(id+"F0.wireOp",EDGE,"E10.7.2"),sQuery(id+"F0.wireOp",EDGE,"E10.8.0"),sQuery(id+"F0.wireOp",EDGE,"E10.8.1"),sQuery(id+"F0.wireOp",EDGE,"E10.8.2"),sQuery(id+"F0.wireOp",EDGE,"E10.9.0"),sQuery(id+"F0.wireOp",EDGE,"E10.9.1"),sQuery(id+"F0.wireOp",EDGE,"E10.9.2"),sQuery(id+"F0.wireOp",EDGE,"E10.10.0"),sQuery(id+"F0.wireOp",EDGE,"E10.10.1"),sQuery(id+"F0.wireOp",EDGE,"E10.10.2"),sQuery(id+"F0.wireOp",EDGE,"E10.11.0"),sQuery(id+"F0.wireOp",EDGE,"E10.11.1"),sQuery(id+"F0.wireOp",EDGE,"E10.11.2"),sQuery(id+"F0.wireOp",EDGE,"E10.12.0"),sQuery(id+"F0.wireOp",EDGE,"E10.12.1"),sQuery(id+"F0.wireOp",EDGE,"E10.12.2"),sQuery(id+"F0.wireOp",EDGE,"E10.13.0"),sQuery(id+"F0.wireOp",EDGE,"E10.13.1"),sQuery(id+"F0.wireOp",EDGE,"E10.13.2"),sQuery(id+"F0.wireOp",EDGE,"E10.14.0"),sQuery(id+"F0.wireOp",EDGE,"E10.14.1"),sQuery(id+"F0.wireOp",EDGE,"E10.14.2"),sQuery(id+"F0.wireOp",EDGE,"E10.15.0"),sQuery(id+"F0.wireOp",EDGE,"E10.15.1"),sQuery(id+"F0.wireOp",EDGE,"E10.15.2"),sQuery(id+"F0.wireOp",EDGE,"E10.16.0"),sQuery(id+"F0.wireOp",EDGE,"E10.16.1"),sQuery(id+"F0.wireOp",EDGE,"E10.16.2"),sQuery(id+"F0.wireOp",EDGE,"E10.17.0"),sQuery(id+"F0.wireOp",EDGE,"E10.17.1"),sQuery(id+"F0.wireOp",EDGE,"E10.17.2"),sQuery(id+"F0.wireOp",EDGE,"E11.filletArc"),sQuery(id+"F0.wireOp",EDGE,"E12.filletArc"),sQuery(id+"F0.wireOp",EDGE,"E13.filletArc"),sQuery(id+"F0.wireOp",EDGE,"E14.filletArc"),sQuery(id+"F0.wireOp",EDGE,"E15.filletArc"),sQuery(id+"F0.wireOp",EDGE,"E16.filletArc"),sQuery(id+"F0.wireOp",EDGE,"E17.filletArc"),sQuery(id+"F0.wireOp",EDGE,"E18.filletArc"),sQuery(id+"F0.wireOp",EDGE,"E19.filletArc"),sQuery(id+"F0.wireOp",EDGE,"E20.filletArc"),sQuery(id+"F0.wireOp",EDGE,"E21.filletArc"),sQuery(id+"F0.wireOp",EDGE,"E22.filletArc"),sQuery(id+"F0.wireOp",EDGE,"E23.filletArc"),sQuery(id+"F0.wireOp",EDGE,"E24.filletArc"),sQuery(id+"F0.wireOp",EDGE,"E25.filletArc"),sQuery(id+"F0.wireOp",EDGE,"E26.filletArc"),sQuery(id+"F0.wireOp",EDGE,"E27.filletArc"),sQuery(id+"F0.wireOp",EDGE,"E28.filletArc"),sQuery(id+"F0.wireOp",EDGE,"E29.filletArc"),sQuery(id+"F0.wireOp",EDGE,"E30.filletArc"),sQuery(id+"F0.wireOp",EDGE,"E31.filletArc"),sQuery(id+"F0.wireOp",EDGE,"E32.filletArc"),sQuery(id+"F0.wireOp",EDGE,"E33.filletArc"),sQuery(id+"F0.wireOp",EDGE,"E34.filletArc"),sQuery(id+"F0.wireOp",EDGE,"E35.filletArc"),sQuery(id+"F0.wireOp",EDGE,"E36.filletArc"),sQuery(id+"F0.wireOp",EDGE,"E37.filletArc"),sQuery(id+"F0.wireOp",EDGE,"E38.filletArc"),sQuery(id+"F0.wireOp",EDGE,"E39.filletArc"),sQuery(id+"F0.wireOp",EDGE,"E40.filletArc"),sQuery(id+"F0.wireOp",EDGE,"E41.filletArc"),sQuery(id+"F0.wireOp",EDGE,"E42.filletArc"),sQuery(id+"F0.wireOp",EDGE,"E43.filletArc"),sQuery(id+"F0.wireOp",EDGE,"E44.filletArc"),sQuery(id+"F0.wireOp",EDGE,"E45.filletArc"),sQuery(id+"F0.wireOp",EDGE,"E46.filletArc")])],"isStart":false}),makeQuery(id+"F3.opExtrude","CAP_FACE",FACE,{"disambiguationData":[OSD([sQuery(id+"F2.wireOp",EDGE,"E47")])],"isStart":false})]});
            var sketch = newSketch(context, id + "F5", { "sketchPlane" : qUnion([Q0])});
            skLineSegment(sketch, "E48.bottom", {"start": v(-25.4, 39.37) * mm, "end": v(-19.05, 39.37) * mm});
            skLineSegment(sketch, "E48.top", {"start": v(-25.4, 38.1) * mm, "end": v(-19.05, 38.1) * mm});
            skLineSegment(sketch, "E48.left", {"start": v(-25.4, 39.37) * mm, "end": v(-25.4, 38.1) * mm});
            skLineSegment(sketch, "E48.right", {"start": v(-19.05, 39.37) * mm, "end": v(-19.05, 38.1) * mm});
            skLineSegment(sketch, "E49.MirrorCS", {"start": v(-25.4, -39.37) * mm, "end": v(-19.05, -39.37) * mm});
            skLineSegment(sketch, "E50.MirrorCS", {"start": v(-25.4, -39.37) * mm, "end": v(-25.4, -38.1) * mm});
            skLineSegment(sketch, "E51.MirrorCS", {"start": v(-19.05, -39.37) * mm, "end": v(-19.05, -38.1) * mm});
            skLineSegment(sketch, "E52.MirrorCS", {"start": v(-25.4, -38.1) * mm, "end": v(-19.05, -38.1) * mm});
            skLineSegment(sketch, "E53.bottom", {"start": v(20.28, 13.97) * mm, "end": v(26.63, 13.97) * mm});
            skLineSegment(sketch, "E53.top", {"start": v(20.28, 12.7) * mm, "end": v(26.63, 12.7) * mm});
            skLineSegment(sketch, "E53.left", {"start": v(20.28, 13.97) * mm, "end": v(20.28, 12.7) * mm});
            skLineSegment(sketch, "E53.right", {"start": v(26.63, 13.97) * mm, "end": v(26.63, 12.7) * mm});
            skLineSegment(sketch, "E54.MirrorCS", {"start": v(20.28, -12.7) * mm, "end": v(26.63, -12.7) * mm});
            skLineSegment(sketch, "E55.MirrorCS", {"start": v(20.28, -13.97) * mm, "end": v(26.63, -13.97) * mm});
            skLineSegment(sketch, "E56.MirrorCS", {"start": v(20.28, -13.97) * mm, "end": v(20.28, -12.7) * mm});
            skLineSegment(sketch, "E57.MirrorCS", {"start": v(26.63, -13.97) * mm, "end": v(26.63, -12.7) * mm});
            skLineSegment(sketch, "E58.bottom", {"start": v(-25.4, 31.75) * mm, "end": v(-19.05, 31.75) * mm});
            skLineSegment(sketch, "E58.top", {"start": v(-25.4, 30.48) * mm, "end": v(-19.05, 30.48) * mm});
            skLineSegment(sketch, "E58.left", {"start": v(-25.4, 31.75) * mm, "end": v(-25.4, 30.48) * mm});
            skLineSegment(sketch, "E58.right", {"start": v(-19.05, 31.75) * mm, "end": v(-19.05, 30.48) * mm});
            skLineSegment(sketch, "E59.bottom", {"start": v(20.28, 21.59) * mm, "end": v(26.63, 21.59) * mm});
            skLineSegment(sketch, "E59.top", {"start": v(20.28, 20.32) * mm, "end": v(26.63, 20.32) * mm});
            skLineSegment(sketch, "E59.left", {"start": v(20.28, 21.59) * mm, "end": v(20.28, 20.32) * mm});
            skLineSegment(sketch, "E59.right", {"start": v(26.63, 21.59) * mm, "end": v(26.63, 20.32) * mm});
            skLineSegment(sketch, "E60.MirrorCS", {"start": v(-25.4, -30.48) * mm, "end": v(-19.05, -30.48) * mm});
            skLineSegment(sketch, "E61.MirrorCS", {"start": v(-25.4, -31.75) * mm, "end": v(-19.05, -31.75) * mm});
            skLineSegment(sketch, "E62.MirrorCS", {"start": v(20.28, -20.32) * mm, "end": v(26.63, -20.32) * mm});
            skLineSegment(sketch, "E63.MirrorCS", {"start": v(20.28, -21.59) * mm, "end": v(26.63, -21.59) * mm});
            skLineSegment(sketch, "E64.MirrorCS", {"start": v(20.28, -21.59) * mm, "end": v(20.28, -20.32) * mm});
            skLineSegment(sketch, "E65.MirrorCS", {"start": v(26.63, -21.59) * mm, "end": v(26.63, -20.32) * mm});
            skLineSegment(sketch, "E66.MirrorCS", {"start": v(-25.4, -31.75) * mm, "end": v(-25.4, -30.48) * mm});
            skLineSegment(sketch, "E67.MirrorCS", {"start": v(-19.05, -31.75) * mm, "end": v(-19.05, -30.48) * mm});
            skSolve(sketch);
        }
        {
            var Q0;
            Q0 = qSketchRegion(id + "F5", true);
            extrude(context, id + "F6", {"entities" : qUnion([Q0]), "operationType" : NewBodyOperationType.REMOVE, "endBound" : BoundingType.THROUGH_ALL, "oppositeDirection" : true, "depth" : 25.4 * mm, "offsetDistance" : 25.4 * mm});
        }
        {
            var Q0;
            Q0=makeQuery(id+"F3.boolean.opBoolean","MERGE",FACE,{"derivedFrom":[makeQuery(id+"F1.opExtrude","CAP_FACE",FACE,{"disambiguationData":[OSD([sQuery(id+"F0.wireOp",EDGE,"E2"),sQuery(id+"F0.wireOp",EDGE,"E3.0"),sQuery(id+"F0.wireOp",EDGE,"E4.trimOffspring"),sQuery(id+"F0.wireOp",EDGE,"E6.1.0"),sQuery(id+"F0.wireOp",EDGE,"E6.2.0"),sQuery(id+"F0.wireOp",EDGE,"E7.3.3.0"),sQuery(id+"F0.wireOp",EDGE,"E7.3.4.0"),sQuery(id+"F0.wireOp",EDGE,"E7.3.5.0"),sQuery(id+"F0.wireOp",EDGE,"E7.3.6.0"),sQuery(id+"F0.wireOp",EDGE,"E7.3.7.0"),sQuery(id+"F0.wireOp",EDGE,"E7.3.8.0"),sQuery(id+"F0.wireOp",EDGE,"E7.3.9.0"),sQuery(id+"F0.wireOp",EDGE,"E7.3.10.0"),sQuery(id+"F0.wireOp",EDGE,"E7.3.11.0"),sQuery(id+"F0.wireOp",EDGE,"E7.3.12.0"),sQuery(id+"F0.wireOp",EDGE,"E7.3.13.0"),sQuery(id+"F0.wireOp",EDGE,"E7.3.14.0"),sQuery(id+"F0.wireOp",EDGE,"E7.3.15.0"),sQuery(id+"F0.wireOp",EDGE,"E7.3.16.0"),sQuery(id+"F0.wireOp",EDGE,"E7.3.17.0"),sQuery(id+"F0.wireOp",EDGE,"E8"),sQuery(id+"F0.wireOp",EDGE,"E9"),sQuery(id+"F0.wireOp",EDGE,"E10.1.0"),sQuery(id+"F0.wireOp",EDGE,"E10.1.1"),sQuery(id+"F0.wireOp",EDGE,"E10.1.2"),sQuery(id+"F0.wireOp",EDGE,"E10.2.0"),sQuery(id+"F0.wireOp",EDGE,"E10.2.1"),sQuery(id+"F0.wireOp",EDGE,"E10.2.2"),sQuery(id+"F0.wireOp",EDGE,"E10.3.0"),sQuery(id+"F0.wireOp",EDGE,"E10.3.1"),sQuery(id+"F0.wireOp",EDGE,"E10.3.2"),sQuery(id+"F0.wireOp",EDGE,"E10.4.0"),sQuery(id+"F0.wireOp",EDGE,"E10.4.1"),sQuery(id+"F0.wireOp",EDGE,"E10.4.2"),sQuery(id+"F0.wireOp",EDGE,"E10.5.0"),sQuery(id+"F0.wireOp",EDGE,"E10.5.1"),sQuery(id+"F0.wireOp",EDGE,"E10.5.2"),sQuery(id+"F0.wireOp",EDGE,"E10.6.0"),sQuery(id+"F0.wireOp",EDGE,"E10.6.1"),sQuery(id+"F0.wireOp",EDGE,"E10.6.2"),sQuery(id+"F0.wireOp",EDGE,"E10.7.0"),sQuery(id+"F0.wireOp",EDGE,"E10.7.1"),sQuery(id+"F0.wireOp",EDGE,"E10.7.2"),sQuery(id+"F0.wireOp",EDGE,"E10.8.0"),sQuery(id+"F0.wireOp",EDGE,"E10.8.1"),sQuery(id+"F0.wireOp",EDGE,"E10.8.2"),sQuery(id+"F0.wireOp",EDGE,"E10.9.0"),sQuery(id+"F0.wireOp",EDGE,"E10.9.1"),sQuery(id+"F0.wireOp",EDGE,"E10.9.2"),sQuery(id+"F0.wireOp",EDGE,"E10.10.0"),sQuery(id+"F0.wireOp",EDGE,"E10.10.1"),sQuery(id+"F0.wireOp",EDGE,"E10.10.2"),sQuery(id+"F0.wireOp",EDGE,"E10.11.0"),sQuery(id+"F0.wireOp",EDGE,"E10.11.1"),sQuery(id+"F0.wireOp",EDGE,"E10.11.2"),sQuery(id+"F0.wireOp",EDGE,"E10.12.0"),sQuery(id+"F0.wireOp",EDGE,"E10.12.1"),sQuery(id+"F0.wireOp",EDGE,"E10.12.2"),sQuery(id+"F0.wireOp",EDGE,"E10.13.0"),sQuery(id+"F0.wireOp",EDGE,"E10.13.1"),sQuery(id+"F0.wireOp",EDGE,"E10.13.2"),sQuery(id+"F0.wireOp",EDGE,"E10.14.0"),sQuery(id+"F0.wireOp",EDGE,"E10.14.1"),sQuery(id+"F0.wireOp",EDGE,"E10.14.2"),sQuery(id+"F0.wireOp",EDGE,"E10.15.0"),sQuery(id+"F0.wireOp",EDGE,"E10.15.1"),sQuery(id+"F0.wireOp",EDGE,"E10.15.2"),sQuery(id+"F0.wireOp",EDGE,"E10.16.0"),sQuery(id+"F0.wireOp",EDGE,"E10.16.1"),sQuery(id+"F0.wireOp",EDGE,"E10.16.2"),sQuery(id+"F0.wireOp",EDGE,"E10.17.0"),sQuery(id+"F0.wireOp",EDGE,"E10.17.1"),sQuery(id+"F0.wireOp",EDGE,"E10.17.2"),sQuery(id+"F0.wireOp",EDGE,"E11.filletArc"),sQuery(id+"F0.wireOp",EDGE,"E12.filletArc"),sQuery(id+"F0.wireOp",EDGE,"E13.filletArc"),sQuery(id+"F0.wireOp",EDGE,"E14.filletArc"),sQuery(id+"F0.wireOp",EDGE,"E15.filletArc"),sQuery(id+"F0.wireOp",EDGE,"E16.filletArc"),sQuery(id+"F0.wireOp",EDGE,"E17.filletArc"),sQuery(id+"F0.wireOp",EDGE,"E18.filletArc"),sQuery(id+"F0.wireOp",EDGE,"E19.filletArc"),sQuery(id+"F0.wireOp",EDGE,"E20.filletArc"),sQuery(id+"F0.wireOp",EDGE,"E21.filletArc"),sQuery(id+"F0.wireOp",EDGE,"E22.filletArc"),sQuery(id+"F0.wireOp",EDGE,"E23.filletArc"),sQuery(id+"F0.wireOp",EDGE,"E24.filletArc"),sQuery(id+"F0.wireOp",EDGE,"E25.filletArc"),sQuery(id+"F0.wireOp",EDGE,"E26.filletArc"),sQuery(id+"F0.wireOp",EDGE,"E27.filletArc"),sQuery(id+"F0.wireOp",EDGE,"E28.filletArc"),sQuery(id+"F0.wireOp",EDGE,"E29.filletArc"),sQuery(id+"F0.wireOp",EDGE,"E30.filletArc"),sQuery(id+"F0.wireOp",EDGE,"E31.filletArc"),sQuery(id+"F0.wireOp",EDGE,"E32.filletArc"),sQuery(id+"F0.wireOp",EDGE,"E33.filletArc"),sQuery(id+"F0.wireOp",EDGE,"E34.filletArc"),sQuery(id+"F0.wireOp",EDGE,"E35.filletArc"),sQuery(id+"F0.wireOp",EDGE,"E36.filletArc"),sQuery(id+"F0.wireOp",EDGE,"E37.filletArc"),sQuery(id+"F0.wireOp",EDGE,"E38.filletArc"),sQuery(id+"F0.wireOp",EDGE,"E39.filletArc"),sQuery(id+"F0.wireOp",EDGE,"E40.filletArc"),sQuery(id+"F0.wireOp",EDGE,"E41.filletArc"),sQuery(id+"F0.wireOp",EDGE,"E42.filletArc"),sQuery(id+"F0.wireOp",EDGE,"E43.filletArc"),sQuery(id+"F0.wireOp",EDGE,"E44.filletArc"),sQuery(id+"F0.wireOp",EDGE,"E45.filletArc"),sQuery(id+"F0.wireOp",EDGE,"E46.filletArc")])],"isStart":false}),makeQuery(id+"F3.opExtrude","CAP_FACE",FACE,{"disambiguationData":[OSD([sQuery(id+"F2.wireOp",EDGE,"E47")])],"isStart":false})]});
            var sketch = newSketch(context, id + "F7", { "sketchPlane" : qUnion([Q0])});
            skLineSegment(sketch, "E68.bottom", {"start": v(-45.4, 6.35) * mm, "end": v(-40.32, 6.35) * mm});
            skLineSegment(sketch, "E68.top", {"start": v(-45.4, -6.35) * mm, "end": v(-40.32, -6.35) * mm});
            skLineSegment(sketch, "E68.left", {"start": v(-45.4, 6.35) * mm, "end": v(-45.4, -6.35) * mm});
            skLineSegment(sketch, "E68.right", {"start": v(-40.32, 6.35) * mm, "end": v(-40.32, -6.35) * mm});
            skSolve(sketch);
        }
        {
            var Q0;
            Q0 = qSketchRegion(id + "F7", true);
            extrude(context, id + "F8", {"entities" : qUnion([Q0]), "operationType" : NewBodyOperationType.ADD, "depth" : 6.35 * mm, "offsetDistance" : 25.4 * mm});
        }
    });
